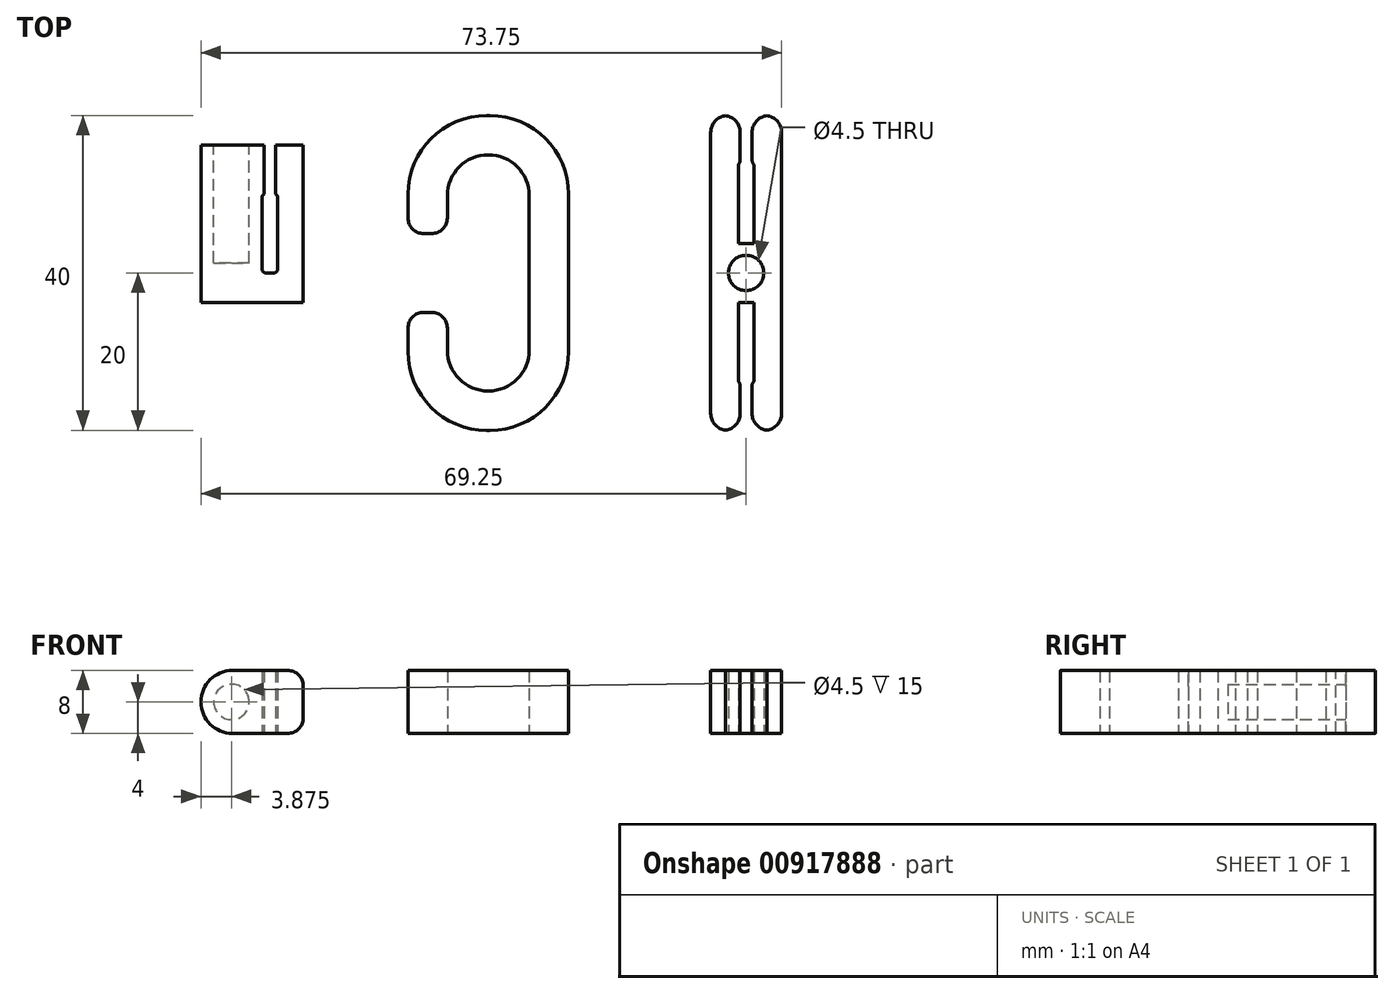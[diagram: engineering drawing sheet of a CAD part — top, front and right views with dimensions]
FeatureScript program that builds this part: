
annotation { "Feature Type Name" : "Feature", "Feature Type Description" : "" }
export const myFeature = defineFeature(function(context is Context, id is Id, definition is map)
    precondition{}
    {
        {
            var Q0;
            Q0=qCreatedBy(makeId("Top.planeOp"),FACE);
            var sketch = newSketch(context, id + "F0", { "sketchPlane" : qUnion([Q0])});
            skLineSegment(sketch, "E0.bottom", {"start": v(5.2, 15) * mm, "end": v(-5.2, 15) * mm});
            skLineSegment(sketch, "E0.top", {"start": v(5.2, -15) * mm, "end": v(-5.2, -15) * mm});
            skLineSegment(sketch, "E0.left", {"start": v(5.2, 15) * mm, "end": v(5.2, -15) * mm});
            skLineSegment(sketch, "E0.right", {"start": v(-5.2, 15) * mm, "end": v(-5.2, 5) * mm});
            skPoint(sketch, "E0.middle", {"position": v(0, 0) * mm});
            skLineSegment(sketch, "E1.bottom", {"start": v(10.2, 20) * mm, "end": v(-10.2, 20) * mm});
            skLineSegment(sketch, "E1.top", {"start": v(10.2, -20) * mm, "end": v(-10.2, -20) * mm});
            skLineSegment(sketch, "E1.left", {"start": v(10.2, 20) * mm, "end": v(10.2, -20) * mm});
            skLineSegment(sketch, "E1.right", {"start": v(-10.2, 20) * mm, "end": v(-10.2, 5) * mm});
            skLineSegment(sketch, "E2", {"start": v(-5.2, 5) * mm, "end": v(-10.2, 5) * mm});
            skLineSegment(sketch, "E3", {"start": v(-5.2, -5) * mm, "end": v(-10.2, -5) * mm});
            skLineSegment(sketch, "E4.trimOffspring", {"start": v(-10.2, -5) * mm, "end": v(-10.2, -20) * mm});
            skLineSegment(sketch, "E5.trimOffspring", {"start": v(-5.2, -5) * mm, "end": v(-5.2, -15) * mm});
            skSolve(sketch);
        }
        {
            var Q0;
            Q0=makeQuery(id+"F0.imprint","IMPRINT",FACE,{"disambiguationData":[TD([[makeQuery(id+"F0.imprint","IMPRINT",EDGE,{"derivedFrom":sQuery(id+"F0.wireOp",EDGE,"E0.bottom")}),-1.0]])]});
            extrude(context, id + "F1", {"entities" : qUnion([Q0]), "depth" : 8 * mm, "offsetDistance" : 25 * mm});
        }
        {
            var Q0;
            Q0=makeQuery(id+"F1.opExtrude","SWEPT_EDGE",EDGE,{"disambiguationData":[OSD([sQuery(id+"F0.wireOp",EDGE,"E0.bottom"),sQuery(id+"F0.wireOp",EDGE,"E0.right")])]});
            var Q1;
            Q1=makeQuery(id+"F1.opExtrude","SWEPT_EDGE",EDGE,{"disambiguationData":[OSD([sQuery(id+"F0.wireOp",EDGE,"E0.bottom"),sQuery(id+"F0.wireOp",EDGE,"E0.left")])]});
            var Q2;
            Q2=makeQuery(id+"F1.opExtrude","SWEPT_EDGE",EDGE,{"disambiguationData":[OSD([sQuery(id+"F0.wireOp",EDGE,"E0.top"),sQuery(id+"F0.wireOp",EDGE,"E5.trimOffspring")])]});
            var Q3;
            Q3=makeQuery(id+"F1.opExtrude","SWEPT_EDGE",EDGE,{"disambiguationData":[OSD([sQuery(id+"F0.wireOp",EDGE,"E0.top"),sQuery(id+"F0.wireOp",EDGE,"E0.left")])]});
            fillet(context, id + "F2", {"entities" : qUnion([Q0, Q1, Q2, Q3]), "radius" : 5.2 * mm, "tangentPropagation" : true, "allowEdgeOverflow" : false});
        }
        {
            var Q0;
            Q0=makeQuery(id+"F1.opExtrude","SWEPT_EDGE",EDGE,{"disambiguationData":[OSD([sQuery(id+"F0.wireOp",EDGE,"E1.bottom"),sQuery(id+"F0.wireOp",EDGE,"E1.right")])]});
            var Q1;
            Q1=makeQuery(id+"F1.opExtrude","SWEPT_EDGE",EDGE,{"disambiguationData":[OSD([sQuery(id+"F0.wireOp",EDGE,"E1.bottom"),sQuery(id+"F0.wireOp",EDGE,"E1.left")])]});
            var Q2;
            Q2=makeQuery(id+"F1.opExtrude","SWEPT_EDGE",EDGE,{"disambiguationData":[OSD([sQuery(id+"F0.wireOp",EDGE,"E1.top"),sQuery(id+"F0.wireOp",EDGE,"E1.left")])]});
            var Q3;
            Q3=makeQuery(id+"F1.opExtrude","SWEPT_EDGE",EDGE,{"disambiguationData":[OSD([sQuery(id+"F0.wireOp",EDGE,"E1.top"),sQuery(id+"F0.wireOp",EDGE,"E4.trimOffspring")])]});
            fillet(context, id + "F3", {"entities" : qUnion([Q0, Q1, Q2, Q3]), "radius" : 10 * mm, "tangentPropagation" : true, "allowEdgeOverflow" : false});
        }
        {
            var Q0;
            Q0=makeQuery(id+"F1.opExtrude","SWEPT_EDGE",EDGE,{"disambiguationData":[OSD([sQuery(id+"F0.wireOp",EDGE,"E1.right"),sQuery(id+"F0.wireOp",EDGE,"E2")])]});
            var Q1;
            Q1=makeQuery(id+"F1.opExtrude","SWEPT_EDGE",EDGE,{"disambiguationData":[OSD([sQuery(id+"F0.wireOp",EDGE,"E0.right"),sQuery(id+"F0.wireOp",EDGE,"E2")])]});
            var Q2;
            Q2=makeQuery(id+"F1.opExtrude","SWEPT_EDGE",EDGE,{"disambiguationData":[OSD([sQuery(id+"F0.wireOp",EDGE,"E3"),sQuery(id+"F0.wireOp",EDGE,"E5.trimOffspring")])]});
            var Q3;
            Q3=makeQuery(id+"F1.opExtrude","SWEPT_EDGE",EDGE,{"disambiguationData":[OSD([sQuery(id+"F0.wireOp",EDGE,"E3"),sQuery(id+"F0.wireOp",EDGE,"E4.trimOffspring")])]});
            fillet(context, id + "F4", {"entities" : qUnion([Q0, Q1, Q2, Q3]), "radius" : 2 * mm, "tangentPropagation" : true, "allowEdgeOverflow" : false});
        }
        {
            var Q0;
            Q0=qCreatedBy(makeId("Top.planeOp"),FACE);
            var sketch = newSketch(context, id + "F5", { "sketchPlane" : qUnion([Q0])});
            skLineSegment(sketch, "E6.bottom", {"start": v(31.75, 20) * mm, "end": v(28.25, 20) * mm});
            skLineSegment(sketch, "E6.top", {"start": v(31.75, -20) * mm, "end": v(28.25, -20) * mm});
            skLineSegment(sketch, "E6.left", {"start": v(31.75, 13.75) * mm, "end": v(31.75, 3.75) * mm});
            skLineSegment(sketch, "E6.right", {"start": v(28.25, 20) * mm, "end": v(28.25, -20) * mm});
            skPoint(sketch, "E6.middle", {"position": v(30, 0) * mm});
            skLineSegment(sketch, "E7.bottom", {"start": v(33.75, 20) * mm, "end": v(37.25, 20) * mm});
            skLineSegment(sketch, "E7.top", {"start": v(33.75, -20) * mm, "end": v(37.25, -20) * mm});
            skLineSegment(sketch, "E7.left", {"start": v(33.75, 13.75) * mm, "end": v(33.75, 3.75) * mm});
            skLineSegment(sketch, "E7.right", {"start": v(37.25, 20) * mm, "end": v(37.25, -20) * mm});
            skPoint(sketch, "E7.middle", {"position": v(35.5, 0) * mm});
            skLineSegment(sketch, "E8.bottom", {"start": v(33.75, 3.75) * mm, "end": v(31.75, 3.75) * mm});
            skLineSegment(sketch, "E8.top", {"start": v(33.75, -3.75) * mm, "end": v(31.75, -3.75) * mm});
            skPoint(sketch, "E8.middle", {"position": v(32.75, 0) * mm});
            skPoint(sketch, "E8.middle.positionSnap0", {"position": v(33.75, 0) * mm});
            skPoint(sketch, "E8.centerSnap0", {"position": v(33.75, 0) * mm});
            skLineSegment(sketch, "E9.trimOffspring", {"start": v(31.75, -3.75) * mm, "end": v(31.75, -13.75) * mm});
            skLineSegment(sketch, "E10.trimOffspring", {"start": v(33.75, -3.75) * mm, "end": v(33.75, -13.75) * mm});
            skLineSegment(sketch, "E11", {"start": v(31.75, -20) * mm, "end": v(32, -20) * mm});
            skLineSegment(sketch, "E12", {"start": v(32, -20) * mm, "end": v(32, -13.75) * mm});
            skLineSegment(sketch, "E13", {"start": v(32, -13.75) * mm, "end": v(31.75, -13.75) * mm});
            skLineSegment(sketch, "E14", {"start": v(33.75, -20) * mm, "end": v(33.5, -20) * mm});
            skLineSegment(sketch, "E15", {"start": v(33.5, -20) * mm, "end": v(33.5, -13.75) * mm});
            skLineSegment(sketch, "E16", {"start": v(33.5, -13.75) * mm, "end": v(33.75, -13.75) * mm});
            skLineSegment(sketch, "E17", {"start": v(32, 20) * mm, "end": v(31.75, 20) * mm});
            skLineSegment(sketch, "E18", {"start": v(32, 13.75) * mm, "end": v(31.75, 13.75) * mm});
            skLineSegment(sketch, "E19", {"start": v(32, 20) * mm, "end": v(32, 13.75) * mm});
            skLineSegment(sketch, "E20", {"start": v(33.75, 20) * mm, "end": v(33.5, 20) * mm});
            skLineSegment(sketch, "E21", {"start": v(33.5, 20) * mm, "end": v(33.5, 13.75) * mm});
            skLineSegment(sketch, "E22", {"start": v(33.5, 13.75) * mm, "end": v(33.75, 13.75) * mm});
            skSolve(sketch);
        }
        {
            var Q0;
            Q0=makeQuery(id+"F5.imprint","IMPRINT",FACE,{"disambiguationData":[TD([[makeQuery(id+"F5.imprint","IMPRINT",EDGE,{"derivedFrom":sQuery(id+"F5.wireOp",EDGE,"E6.bottom")}),1.0]])]});
            extrude(context, id + "F6", {"entities" : qUnion([Q0]), "depth" : 8 * mm, "offsetDistance" : 25 * mm});
        }
        {
            var Q0;
            Q0=makeQuery(id+"F6.opExtrude","CAP_FACE",FACE,{"disambiguationData":[OSD([sQuery(id+"F5.wireOp",EDGE,"E6.bottom"),sQuery(id+"F5.wireOp",EDGE,"E6.top"),sQuery(id+"F5.wireOp",EDGE,"E6.left"),sQuery(id+"F5.wireOp",EDGE,"E6.right"),sQuery(id+"F5.wireOp",EDGE,"E7.bottom"),sQuery(id+"F5.wireOp",EDGE,"E7.top"),sQuery(id+"F5.wireOp",EDGE,"E7.left"),sQuery(id+"F5.wireOp",EDGE,"E7.right"),sQuery(id+"F5.wireOp",EDGE,"E8.bottom"),sQuery(id+"F5.wireOp",EDGE,"E8.top"),sQuery(id+"F5.wireOp",EDGE,"E9.trimOffspring"),sQuery(id+"F5.wireOp",EDGE,"E10.trimOffspring"),sQuery(id+"F5.wireOp",EDGE,"E11"),sQuery(id+"F5.wireOp",EDGE,"E12"),sQuery(id+"F5.wireOp",EDGE,"E13"),sQuery(id+"F5.wireOp",EDGE,"E14"),sQuery(id+"F5.wireOp",EDGE,"E15"),sQuery(id+"F5.wireOp",EDGE,"E16"),sQuery(id+"F5.wireOp",EDGE,"E17"),sQuery(id+"F5.wireOp",EDGE,"E18"),sQuery(id+"F5.wireOp",EDGE,"E19"),sQuery(id+"F5.wireOp",EDGE,"E20"),sQuery(id+"F5.wireOp",EDGE,"E21"),sQuery(id+"F5.wireOp",EDGE,"E22")])],"isStart":true});
            var sketch = newSketch(context, id + "F7", { "sketchPlane" : qUnion([Q0])});
            skCircle(sketch, "E23", {"center": v(32.75, 0) * mm, "radius": 2.25 * mm});
            skPoint(sketch, "E23.centerSnap0", {"position": v(32.75, 3.75) * mm});
            skSolve(sketch);
        }
        {
            var Q0;
            Q0=makeQuery(id+"F7.imprint","IMPRINT",FACE,{"disambiguationData":[TD([[makeQuery(id+"F7.imprint","IMPRINT",EDGE,{"derivedFrom":sQuery(id+"F7.wireOp",EDGE,"E23")}),1.0]])]});
            extrude(context, id + "F8", {"entities" : qUnion([Q0]), "operationType" : NewBodyOperationType.REMOVE, "endBound" : BoundingType.UP_TO_NEXT, "oppositeDirection" : true, "depth" : 6 * mm, "offsetDistance" : 25 * mm});
        }
        {
            var Q0;
            Q0=makeQuery(id+"F6.opExtrude","SWEPT_EDGE",EDGE,{"disambiguationData":[OSD([sQuery(id+"F5.wireOp",EDGE,"E6.top"),sQuery(id+"F5.wireOp",EDGE,"E6.right")])]});
            var Q1;
            Q1=makeQuery(id+"F6.opExtrude","SWEPT_EDGE",EDGE,{"disambiguationData":[OSD([sQuery(id+"F5.wireOp",EDGE,"E11"),sQuery(id+"F5.wireOp",EDGE,"E12")])]});
            var Q2;
            Q2=makeQuery(id+"F6.opExtrude","SWEPT_EDGE",EDGE,{"disambiguationData":[OSD([sQuery(id+"F5.wireOp",EDGE,"E7.top"),sQuery(id+"F5.wireOp",EDGE,"E7.right")])]});
            var Q3;
            Q3=makeQuery(id+"F6.opExtrude","SWEPT_EDGE",EDGE,{"disambiguationData":[OSD([sQuery(id+"F5.wireOp",EDGE,"E14"),sQuery(id+"F5.wireOp",EDGE,"E15")])]});
            var Q4;
            Q4=makeQuery(id+"F6.opExtrude","SWEPT_EDGE",EDGE,{"disambiguationData":[OSD([sQuery(id+"F5.wireOp",EDGE,"E7.bottom"),sQuery(id+"F5.wireOp",EDGE,"E7.right")])]});
            var Q5;
            Q5=makeQuery(id+"F6.opExtrude","SWEPT_EDGE",EDGE,{"disambiguationData":[OSD([sQuery(id+"F5.wireOp",EDGE,"E20"),sQuery(id+"F5.wireOp",EDGE,"E21")])]});
            var Q6;
            Q6=makeQuery(id+"F6.opExtrude","SWEPT_EDGE",EDGE,{"disambiguationData":[OSD([sQuery(id+"F5.wireOp",EDGE,"E17"),sQuery(id+"F5.wireOp",EDGE,"E19")])]});
            var Q7;
            Q7=makeQuery(id+"F6.opExtrude","SWEPT_EDGE",EDGE,{"disambiguationData":[OSD([sQuery(id+"F5.wireOp",EDGE,"E6.bottom"),sQuery(id+"F5.wireOp",EDGE,"E6.right")])]});
            fillet(context, id + "F9", {"entities" : qUnion([Q0, Q1, Q2, Q3, Q4, Q5, Q6, Q7]), "radius" : 2.15 * mm, "tangentPropagation" : true, "allowEdgeOverflow" : false});
        }
        {
            var Q0;
            Q0=makeQuery(id+"F6.opExtrude","SWEPT_EDGE",EDGE,{"disambiguationData":[OSD([sQuery(id+"F5.wireOp",EDGE,"E15"),sQuery(id+"F5.wireOp",EDGE,"E16")])]});
            var Q1;
            Q1=makeQuery(id+"F6.opExtrude","SWEPT_EDGE",EDGE,{"disambiguationData":[OSD([sQuery(id+"F5.wireOp",EDGE,"E12"),sQuery(id+"F5.wireOp",EDGE,"E13")])]});
            var Q2;
            Q2=makeQuery(id+"F6.opExtrude","SWEPT_EDGE",EDGE,{"disambiguationData":[OSD([sQuery(id+"F5.wireOp",EDGE,"E18"),sQuery(id+"F5.wireOp",EDGE,"E19")])]});
            var Q3;
            Q3=makeQuery(id+"F6.opExtrude","SWEPT_EDGE",EDGE,{"disambiguationData":[OSD([sQuery(id+"F5.wireOp",EDGE,"E21"),sQuery(id+"F5.wireOp",EDGE,"E22")])]});
            fillet(context, id + "F10", {"entities" : qUnion([Q0, Q1, Q2, Q3]), "radius" : 1 * mm, "tangentPropagation" : true, "allowEdgeOverflow" : false});
        }
        {
            var Q0;
            Q0=qCreatedBy(makeId("Top.planeOp"),FACE);
            var sketch = newSketch(context, id + "F11", { "sketchPlane" : qUnion([Q0])});
            skLineSegment(sketch, "E24.bottom", {"start": v(-23.5, 16.25) * mm, "end": v(-27, 16.25) * mm});
            skLineSegment(sketch, "E24.top", {"start": v(-23.5, -3.75) * mm, "end": v(-36.5, -3.75) * mm});
            skLineSegment(sketch, "E24.left", {"start": v(-23.5, 16.25) * mm, "end": v(-23.5, -3.75) * mm});
            skLineSegment(sketch, "E24.right", {"start": v(-36.5, 16.25) * mm, "end": v(-36.5, -3.75) * mm});
            skPoint(sketch, "E24.middle", {"position": v(-30, 6.25) * mm});
            skLineSegment(sketch, "E25", {"start": v(-27, 16.25) * mm, "end": v(-27, 10) * mm});
            skLineSegment(sketch, "E26", {"start": v(-27, 10) * mm, "end": v(-26.75, 10) * mm});
            skLineSegment(sketch, "E27", {"start": v(-26.75, 10) * mm, "end": v(-26.75, 0) * mm});
            skLineSegment(sketch, "E28", {"start": v(-26.75, 0) * mm, "end": v(-28.75, 0) * mm});
            skLineSegment(sketch, "E29", {"start": v(-28.75, 0) * mm, "end": v(-28.75, 10) * mm});
            skLineSegment(sketch, "E30", {"start": v(-28.75, 10) * mm, "end": v(-28.5, 10) * mm});
            skLineSegment(sketch, "E31", {"start": v(-28.5, 10) * mm, "end": v(-28.5, 16.25) * mm});
            skLineSegment(sketch, "E32.trimOffspring", {"start": v(-28.5, 16.25) * mm, "end": v(-36.5, 16.25) * mm});
            skSolve(sketch);
        }
        {
            var Q0;
            Q0 = qSketchRegion(id + "F11", true);
            extrude(context, id + "F12", {"entities" : qUnion([Q0]), "depth" : 8 * mm, "offsetDistance" : 25 * mm});
        }
        {
            var Q0;
            Q0=makeQuery(id+"F12.opExtrude","SWEPT_FACE",FACE,{"disambiguationData":[OSD([sQuery(id+"F11.wireOp",EDGE,"E32.trimOffspring")])]});
            var sketch = newSketch(context, id + "F13", { "sketchPlane" : qUnion([Q0])});
            skCircle(sketch, "E33", {"center": v(32.63, 4) * mm, "radius": 2.25 * mm});
            skSolve(sketch);
        }
        {
            var Q0;
            Q0=makeQuery(id+"F13.imprint","IMPRINT",FACE,{"disambiguationData":[TD([[makeQuery(id+"F13.imprint","IMPRINT",EDGE,{"derivedFrom":sQuery(id+"F13.wireOp",EDGE,"E33")}),1.0]])]});
            extrude(context, id + "F14", {"entities" : qUnion([Q0]), "operationType" : NewBodyOperationType.REMOVE, "oppositeDirection" : true, "depth" : 15 * mm, "offsetDistance" : 25 * mm});
        }
        {
            var Q0;
            Q0=makeQuery(id+"F12.opExtrude","CAP_EDGE",EDGE,{"disambiguationData":[OSD([sQuery(id+"F11.wireOp",EDGE,"E24.right")])],"isStart":false});
            var Q1;
            Q1=makeQuery(id+"F12.opExtrude","CAP_EDGE",EDGE,{"disambiguationData":[OSD([sQuery(id+"F11.wireOp",EDGE,"E24.right")])],"isStart":true});
            fillet(context, id + "F15", {"entities" : qUnion([Q0, Q1]), "radius" : 4 * mm, "tangentPropagation" : true, "allowEdgeOverflow" : false});
        }
        {
            var Q0;
            Q0=makeQuery(id+"F12.opExtrude","SWEPT_EDGE",EDGE,{"disambiguationData":[OSD([sQuery(id+"F11.wireOp",EDGE,"E26"),sQuery(id+"F11.wireOp",EDGE,"E27")])]});
            var Q1;
            Q1=makeQuery(id+"F12.opExtrude","SWEPT_EDGE",EDGE,{"disambiguationData":[OSD([sQuery(id+"F11.wireOp",EDGE,"E29"),sQuery(id+"F11.wireOp",EDGE,"E30")])]});
            var Q2;
            {var subQ0=sQuery(id+"F0.wireOp",EDGE,"E1.right");Q2=makeQuery(id+"F4.opFillet","BLEND_EDGE",EDGE,{"blendedFrom":[makeQuery(id+"F1.opExtrude","SWEPT_EDGE",EDGE,{"disambiguationData":[OSD([subQ0,sQuery(id+"F0.wireOp",EDGE,"E2")])]}),makeQuery(id+"F1.opExtrude","SWEPT_FACE",FACE,{"disambiguationData":[OSD([subQ0])]})],"blendedInto":[makeQuery(id+"F1.opExtrude","SWEPT_FACE",FACE,{"disambiguationData":[OSD([subQ0])]})]});}
            var Q3;
            Q3=makeQuery(id+"F12.opExtrude","SWEPT_EDGE",EDGE,{"disambiguationData":[OSD([sQuery(id+"F11.wireOp",EDGE,"E28"),sQuery(id+"F11.wireOp",EDGE,"E29")])]});
            var Q4;
            Q4=makeQuery(id+"F12.opExtrude","SWEPT_EDGE",EDGE,{"disambiguationData":[OSD([sQuery(id+"F11.wireOp",EDGE,"E27"),sQuery(id+"F11.wireOp",EDGE,"E28")])]});
            fillet(context, id + "F16", {"entities" : qUnion([Q0, Q1, Q2, Q3, Q4]), "radius" : 0.5 * mm, "tangentPropagation" : true, "allowEdgeOverflow" : false});
        }
        {
            var Q0;
            Q0=makeQuery(id+"F12.opExtrude","CAP_EDGE",EDGE,{"disambiguationData":[OSD([sQuery(id+"F11.wireOp",EDGE,"E24.left")])],"isStart":false});
            var Q1;
            Q1=makeQuery(id+"F12.opExtrude","CAP_EDGE",EDGE,{"disambiguationData":[OSD([sQuery(id+"F11.wireOp",EDGE,"E24.left")])],"isStart":true});
            fillet(context, id + "F17", {"entities" : qUnion([Q0, Q1]), "radius" : 2 * mm, "tangentPropagation" : true, "allowEdgeOverflow" : false});
        }
    });
